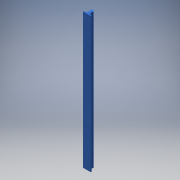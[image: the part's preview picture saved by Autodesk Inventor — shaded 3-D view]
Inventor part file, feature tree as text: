
AUTODESK INVENTOR PART (.ipt)
format: ipt  version: 2018 (Build 220112000, 112)  size: 141,312 bytes
history: native  units: mm
features: sketch x2, other x1, extrude x1, hole x1
ambient origin geometry x8: Origin, YZ Plane, XZ Plane, XY Plane, X Axis, Y Axis, Z Axis, Center Point
bodies: Body1 (feature_tree)
feature tree (5):
  other  "Sólido1"
  extrude  "Extrusão1"  Depth=25.0mm
  hole  "Furo1"  [1 undecoded]
  sketch  "Esboço1"  dims[d6=16.0mm d7=25.0mm]
  sketch  "Esboço3"  dims[d8=18.5mm d9=11.7mm d10=8.0mm d11=30.0deg d12=30.0deg d13=5.0mm d14=40.0mm d15=700.0mm d16=0.0mm d18=15.0mm d19=15.0mm d20=5.5mm d21=5.5mm d22=20.0mm d28=5.5mm d29=6.0mm d30=4.0mm d31=2.0mm d32=90.0deg d33=8.0mm d34=20.594885mm]
note: 1 required parameter value undecoded (feature->parameter linkage not recoverable at this tier; creation-order binding heuristic only, values carry confidence <= 0.55)
